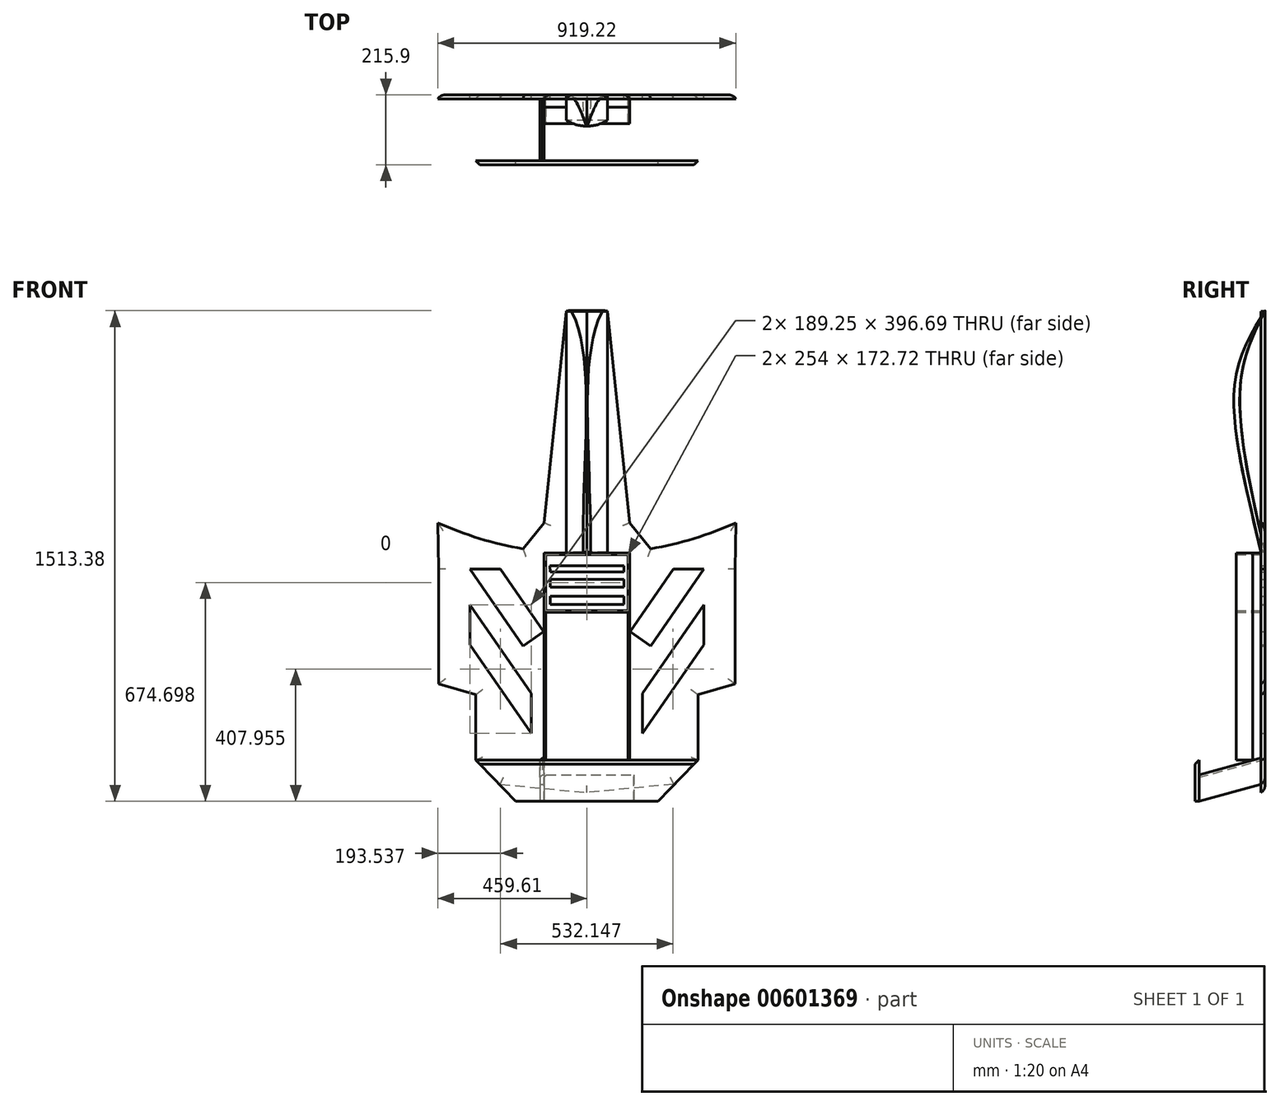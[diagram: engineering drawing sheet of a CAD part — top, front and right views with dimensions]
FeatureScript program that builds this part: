
annotation { "Feature Type Name" : "Feature", "Feature Type Description" : "" }
export const myFeature = defineFeature(function(context is Context, id is Id, definition is map)
    precondition{}
    {
        {
            var Q0;
            Q0=qCreatedBy(makeId("Front.planeOp"),FACE);
            var sketch = newSketch(context, id + "F0", { "sketchPlane" : qUnion([Q0])});
            skLineSegment(sketch, "E0.bottom", {"start": v(-87.15, 1010.87) * mm, "end": v(0, 1010.87) * mm});
            skLineSegment(sketch, "E0.top", {"start": v(-342.9, -81.33) * mm, "end": v(0, -81.33) * mm});
            skLineSegment(sketch, "E0.left", {"start": v(-457.2, 439.97) * mm, "end": v(-457.2, 86.3) * mm});
            skLineSegment(sketch, "E0.right", {"start": v(0, 1010.87) * mm, "end": v(0, -81.33) * mm});
            skLineSegment(sketch, "E1", {"start": v(-457.2, 86.3) * mm, "end": v(-342.9, 52.88) * mm});
            skLineSegment(sketch, "E2", {"start": v(-342.9, 52.88) * mm, "end": v(-342.9, -81.33) * mm});
            skPoint(sketch, "E3.start.orphan", {"position": v(-457.2, 502.87) * mm});
            skPoint(sketch, "E4.start.orphan", {"position": v(-197.03, 542.03) * mm});
            skLineSegment(sketch, "E5", {"start": v(-197.03, 502.87) * mm, "end": v(-132.27, 582.92) * mm});
            skLineSegment(sketch, "E6", {"start": v(-132.27, 582.92) * mm, "end": v(-87.15, 1010.87) * mm});
            skPoint(sketch, "E7.orphan", {"position": v(-457.2, -81.33) * mm});
            skLineSegment(sketch, "E8.MirrorCS", {"start": v(197.03, 502.87) * mm, "end": v(132.27, 582.92) * mm});
            skPoint(sketch, "E9.MirrorP", {"position": v(197.03, 542.03) * mm});
            skLineSegment(sketch, "E10.MirrorCS", {"start": v(87.15, 1010.87) * mm, "end": v(0, 1010.87) * mm});
            skLineSegment(sketch, "E11.MirrorCS", {"start": v(342.9, 52.88) * mm, "end": v(342.9, -81.33) * mm});
            skLineSegment(sketch, "E12.MirrorCS", {"start": v(457.2, 86.3) * mm, "end": v(342.9, 52.88) * mm});
            skPoint(sketch, "E13.MirrorP", {"position": v(457.2, -81.33) * mm});
            skPoint(sketch, "E14.MirrorP", {"position": v(457.2, 502.87) * mm});
            skLineSegment(sketch, "E15.MirrorCS", {"start": v(342.9, -81.33) * mm, "end": v(0, -81.33) * mm});
            skLineSegment(sketch, "E16.MirrorCS", {"start": v(457.2, 439.97) * mm, "end": v(457.2, 86.3) * mm});
            skLineSegment(sketch, "E17.MirrorCS", {"start": v(132.27, 582.92) * mm, "end": v(87.15, 1010.87) * mm});
            skArc(sketch, "E18", {"start": v(-197.03, 502.87) * mm, "mid": v(-330.75, 534.92) * mm, "end": v(-459.6, 582.92) * mm});
            skLineSegment(sketch, "E19", {"start": v(-457.2, 439.97) * mm, "end": v(-459.6, 582.92) * mm});
            skPoint(sketch, "E20.center.orphan", {"position": v(-457.2, 1010.87) * mm});
            skArc(sketch, "E21.MirrorCS", {"start": v(197.03, 502.87) * mm, "mid": v(330.75, 534.92) * mm, "end": v(459.6, 582.92) * mm});
            skLineSegment(sketch, "E22.MirrorCS", {"start": v(457.2, 439.97) * mm, "end": v(459.6, 582.92) * mm});
            skLineSegment(sketch, "E23", {"start": v(132.27, 582.92) * mm, "end": v(63.5, 1235.16) * mm});
            skLineSegment(sketch, "E24", {"start": v(0, 1235.16) * mm, "end": v(63.5, 1235.16) * mm});
            skLineSegment(sketch, "E25", {"start": v(0, 1235.16) * mm, "end": v(-63.5, 1235.16) * mm});
            skPoint(sketch, "E26.orphan", {"position": v(-63.5, 1235.16) * mm});
            skLineSegment(sketch, "E27", {"start": v(-63.5, 1235.16) * mm, "end": v(-87.15, 1010.87) * mm});
            skLineSegment(sketch, "E28", {"start": v(0, -81.33) * mm, "end": v(0, -248.97) * mm});
            skLineSegment(sketch, "E29", {"start": v(-342.9, -81.33) * mm, "end": v(-342.9, -148.64) * mm});
            skLineSegment(sketch, "E30", {"start": v(-267.1, -223.25) * mm, "end": v(0, -248.97) * mm});
            skPoint(sketch, "E31.end.orphan", {"position": v(-267.1, -215.95) * mm});
            skLineSegment(sketch, "E32", {"start": v(-342.9, -148.64) * mm, "end": v(-267.1, -223.25) * mm});
            skPoint(sketch, "E33.orphan", {"position": v(-342.9, -215.95) * mm});
            skLineSegment(sketch, "E34.MirrorCS", {"start": v(342.9, -81.33) * mm, "end": v(342.9, -148.64) * mm});
            skLineSegment(sketch, "E35.MirrorCS", {"start": v(342.9, -148.64) * mm, "end": v(267.1, -223.25) * mm});
            skLineSegment(sketch, "E36.MirrorCS", {"start": v(267.1, -223.25) * mm, "end": v(0, -248.97) * mm});
            skLineSegment(sketch, "E37", {"start": v(197.03, 203.43) * mm, "end": v(133.45, 247.43) * mm});
            skLineSegment(sketch, "E38", {"start": v(133.45, 247.43) * mm, "end": v(266.67, 439.97) * mm});
            skLineSegment(sketch, "E39", {"start": v(266.67, 439.97) * mm, "end": v(360.7, 439.97) * mm});
            skLineSegment(sketch, "E40.MirrorCS", {"start": v(-133.45, 247.43) * mm, "end": v(-266.67, 439.97) * mm});
            skLineSegment(sketch, "E41.MirrorCS", {"start": v(-197.03, 203.43) * mm, "end": v(-133.45, 247.43) * mm});
            skLineSegment(sketch, "E42.MirrorCS", {"start": v(-266.67, 439.97) * mm, "end": v(-360.7, 439.97) * mm});
            skLineSegment(sketch, "E43", {"start": v(360.7, 439.97) * mm, "end": v(197.03, 203.43) * mm});
            skLineSegment(sketch, "E44", {"start": v(-360.7, 439.97) * mm, "end": v(-197.03, 203.43) * mm});
            skLineSegment(sketch, "E45", {"start": v(171.45, 57.15) * mm, "end": v(360.7, 330.66) * mm});
            skPoint(sketch, "E45.startSnap0", {"position": v(171.45, -81.33) * mm});
            skLineSegment(sketch, "E46", {"start": v(360.7, 330.66) * mm, "end": v(360.7, 207.48) * mm});
            skLineSegment(sketch, "E47", {"start": v(360.7, 207.48) * mm, "end": v(171.45, -66.03) * mm});
            skLineSegment(sketch, "E48", {"start": v(171.45, 57.15) * mm, "end": v(171.45, -66.03) * mm});
            skLineSegment(sketch, "E49.MirrorCS", {"start": v(-171.45, 57.15) * mm, "end": v(-360.7, 330.66) * mm});
            skLineSegment(sketch, "E50.MirrorCS", {"start": v(-360.7, 207.48) * mm, "end": v(-171.45, -66.03) * mm});
            skLineSegment(sketch, "E51.MirrorCS", {"start": v(-171.45, 57.15) * mm, "end": v(-171.45, -66.03) * mm});
            skLineSegment(sketch, "E52.MirrorCS", {"start": v(-360.7, 330.66) * mm, "end": v(-360.7, 207.48) * mm});
            skLineSegment(sketch, "E53", {"start": v(-114.3, 450.83) * mm, "end": v(114.3, 450.83) * mm});
            skLineSegment(sketch, "E54", {"start": v(114.3, 450.83) * mm, "end": v(114.3, 431.4) * mm});
            skLineSegment(sketch, "E55", {"start": v(114.3, 431.4) * mm, "end": v(-112.92, 431.4) * mm});
            skLineSegment(sketch, "E56", {"start": v(-112.92, 431.4) * mm, "end": v(-114.3, 450.83) * mm});
            skLineSegment(sketch, "E57", {"start": v(-112.92, 408.42) * mm, "end": v(-112.92, 384.28) * mm});
            skLineSegment(sketch, "E58", {"start": v(-112.92, 384.28) * mm, "end": v(114.3, 384.28) * mm});
            skLineSegment(sketch, "E59", {"start": v(114.3, 384.28) * mm, "end": v(114.3, 408.42) * mm});
            skLineSegment(sketch, "E60", {"start": v(114.3, 408.42) * mm, "end": v(-112.92, 408.42) * mm});
            skLineSegment(sketch, "E61", {"start": v(-112.92, 356.37) * mm, "end": v(-112.92, 330.7) * mm});
            skLineSegment(sketch, "E62", {"start": v(-112.92, 330.7) * mm, "end": v(114.3, 330.7) * mm});
            skLineSegment(sketch, "E63", {"start": v(114.3, 330.7) * mm, "end": v(114.3, 356.37) * mm});
            skLineSegment(sketch, "E64", {"start": v(114.3, 356.37) * mm, "end": v(-112.92, 356.37) * mm});
            skSolve(sketch);
        }
        {
            var Q0;
            Q0=qCreatedBy(makeId("Right.planeOp"),FACE);
            var sketch = newSketch(context, id + "F1", { "sketchPlane" : qUnion([Q0])});
            skLineSegment(sketch, "E65", {"start": v(0, -172.72) * mm, "end": v(-76.2, -172.72) * mm});
            skLineSegment(sketch, "E66", {"start": v(-76.2, -172.72) * mm, "end": v(-76.2, 0) * mm});
            skLineSegment(sketch, "E67", {"start": v(-76.2, 0) * mm, "end": v(0, 0) * mm});
            skLineSegment(sketch, "E68", {"start": v(0, 492.63) * mm, "end": v(-12.7, 492.63) * mm});
            skPoint(sketch, "E69.center.orphan", {"position": v(0, 1010.95) * mm});
            skPoint(sketch, "E70.center.orphan", {"position": v(0, -148.77) * mm});
            skFitSpline(sketch, "E71", {"points": [v(0, 492.63) * mm, v(-76.2, 1010.95) * mm, v(0, 1236.69) * mm], "startDerivative": vector(-222.18, 959.65) * mm, "endDerivative": vector(252.99, 498.58) * mm});
            skFitSpline(sketch, "E72", {"points": [v(0, 1237.74) * mm, v(-93.66, 1010.95) * mm, v(-12.7, 492.63) * mm], "startDerivative": vector(-301.04, -493.75) * mm, "endDerivative": vector(220.2, -966.97) * mm});
            skLineSegment(sketch, "E73", {"start": v(-12.7, 492.63) * mm, "end": v(-12.7, -249.15) * mm});
            skLineSegment(sketch, "E74", {"start": v(0, -249.15) * mm, "end": v(-12.7, -249.15) * mm});
            skPoint(sketch, "E75.end.orphan", {"position": v(0, -250.54) * mm});
            skPoint(sketch, "E76.orphan", {"position": v(-12.7, -250.54) * mm});
            skLineSegment(sketch, "E77", {"start": v(0, 492.63) * mm, "end": v(0, -249.15) * mm});
            skLineSegment(sketch, "E78", {"start": v(0, 1236.69) * mm, "end": v(0, 1237.74) * mm});
            skPoint(sketch, "E79.end.orphan", {"position": v(0, -426.72) * mm});
            skPoint(sketch, "E79.start.orphan", {"position": v(-76.2, -426.72) * mm});
            skSolve(sketch);
        }
        {
            var Q0;
            Q0=makeQuery(id+"F0.imprint","IMPRINT",FACE,{"disambiguationData":[TD([[makeQuery(id+"F0.imprint","IMPRINT",EDGE,{"derivedFrom":sQuery(id+"F0.wireOp",EDGE,"E0.right")}),1.0]])]});
            var Q1;
            Q1=makeQuery(id+"F0.imprint","IMPRINT",FACE,{"disambiguationData":[TD([[makeQuery(id+"F0.imprint","IMPRINT",EDGE,{"derivedFrom":sQuery(id+"F0.wireOp",EDGE,"E0.bottom")}),-1.0]])]});
            var Q2;
            Q2=makeQuery(id+"F0.imprint","IMPRINT",FACE,{"disambiguationData":[TD([[makeQuery(id+"F0.imprint","IMPRINT",EDGE,{"derivedFrom":sQuery(id+"F0.wireOp",EDGE,"E0.top")}),-1.0]])]});
            var Q3;
            Q3=makeQuery(id+"F0.imprint","IMPRINT",FACE,{"disambiguationData":[TD([[makeQuery(id+"F0.imprint","IMPRINT",EDGE,{"derivedFrom":sQuery(id+"F0.wireOp",EDGE,"E15.MirrorCS")}),1.0]])]});
            var Q4;
            Q4=makeQuery(id+"F0.imprint","IMPRINT",FACE,{"disambiguationData":[TD([[makeQuery(id+"F0.imprint","IMPRINT",EDGE,{"derivedFrom":sQuery(id+"F0.wireOp",EDGE,"E0.bottom")}),1.0]])]});
            extrude(context, id + "F2", {"entities" : qUnion([Q0, Q1, Q2, Q3, Q4]), "depth" : 12.7 * mm, "offsetDistance" : 25.4 * mm, "hasSecondDirection" : true, "secondDirectionOppositeDirection" : false, "secondDirectionDepth" : 0 * mm});
        }
        {
            var Q0;
            Q0=makeQuery(id+"F1.imprint","IMPRINT",FACE,{"disambiguationData":[TD([[makeQuery(id+"F1.imprint","IMPRINT",EDGE,{"derivedFrom":sQuery(id+"F1.wireOp",EDGE,"E68")}),-1.0]])]});
            extrude(context, id + "F3", {"entities" : qUnion([Q0]), "depth" : 63.5 * mm, "offsetDistance" : 25.4 * mm});
        }
        {
            var Q0;
            Q0=makeQuery(id+"F3.opExtrude","CAP_FACE",FACE,{"disambiguationData":[OSD([sQuery(id+"F1.wireOp",EDGE,"E68"),sQuery(id+"F1.wireOp",EDGE,"E71"),sQuery(id+"F1.wireOp",EDGE,"E72"),sQuery(id+"F1.wireOp",EDGE,"E78")])],"isStart":true});
            extrude(context, id + "F4", {"entities" : qUnion([Q0]), "depth" : 63.5 * mm, "offsetDistance" : 25.4 * mm});
        }
        {
            var Q0;
            Q0=makeQuery(id+"F2.opExtrude","CAP_FACE",FACE,{"disambiguationData":[OSD([sQuery(id+"F0.wireOp",EDGE,"E0.left"),sQuery(id+"F0.wireOp",EDGE,"E1"),sQuery(id+"F0.wireOp",EDGE,"E2"),sQuery(id+"F0.wireOp",EDGE,"E5"),sQuery(id+"F0.wireOp",EDGE,"E8.MirrorCS"),sQuery(id+"F0.wireOp",EDGE,"E11.MirrorCS"),sQuery(id+"F0.wireOp",EDGE,"E12.MirrorCS"),sQuery(id+"F0.wireOp",EDGE,"E16.MirrorCS"),sQuery(id+"F0.wireOp",EDGE,"E18"),sQuery(id+"F0.wireOp",EDGE,"E19"),sQuery(id+"F0.wireOp",EDGE,"E21.MirrorCS"),sQuery(id+"F0.wireOp",EDGE,"E22.MirrorCS"),sQuery(id+"F0.wireOp",EDGE,"E6"),sQuery(id+"F0.wireOp",EDGE,"E23"),sQuery(id+"F0.wireOp",EDGE,"E24"),sQuery(id+"F0.wireOp",EDGE,"E25"),sQuery(id+"F0.wireOp",EDGE,"E27"),sQuery(id+"F0.wireOp",EDGE,"E29"),sQuery(id+"F0.wireOp",EDGE,"E30"),sQuery(id+"F0.wireOp",EDGE,"E32"),sQuery(id+"F0.wireOp",EDGE,"E34.MirrorCS"),sQuery(id+"F0.wireOp",EDGE,"E35.MirrorCS"),sQuery(id+"F0.wireOp",EDGE,"E36.MirrorCS")])],"isStart":false});
            var sketch = newSketch(context, id + "F5", { "sketchPlane" : qUnion([Q0])});
            skLineSegment(sketch, "E80", {"start": v(0, 485.42) * mm, "end": v(-127, 485.42) * mm});
            skLineSegment(sketch, "E81", {"start": v(-127, 485.42) * mm, "end": v(-127, 312.7) * mm});
            skLineSegment(sketch, "E82", {"start": v(-127, 312.7) * mm, "end": v(127, 312.7) * mm});
            skLineSegment(sketch, "E83", {"start": v(127, 312.7) * mm, "end": v(127, 485.42) * mm});
            skLineSegment(sketch, "E84", {"start": v(127, 485.42) * mm, "end": v(0, 485.42) * mm});
            skLineSegment(sketch, "E85", {"start": v(-132.08, 485.42) * mm, "end": v(-132.08, 307.62) * mm});
            skLineSegment(sketch, "E86", {"start": v(-132.08, 307.62) * mm, "end": v(132.08, 307.62) * mm});
            skLineSegment(sketch, "E87", {"start": v(132.08, 307.62) * mm, "end": v(132.08, 490.5) * mm});
            skLineSegment(sketch, "E88", {"start": v(132.08, 490.5) * mm, "end": v(-132.08, 490.5) * mm});
            skLineSegment(sketch, "E89", {"start": v(-132.08, 490.5) * mm, "end": v(-132.08, 485.42) * mm});
            skLineSegment(sketch, "E90", {"start": v(132.08, 307.62) * mm, "end": v(132.08, -236.25) * mm});
            skLineSegment(sketch, "E91", {"start": v(-132.08, 307.62) * mm, "end": v(-132.08, -236.25) * mm});
            skLineSegment(sketch, "E92", {"start": v(-127, 312.7) * mm, "end": v(-127, -236.25) * mm});
            skLineSegment(sketch, "E93", {"start": v(127, 312.7) * mm, "end": v(127, -90.76) * mm});
            skLineSegment(sketch, "E94", {"start": v(127, -90.76) * mm, "end": v(127, -236.25) * mm});
            skLineSegment(sketch, "E95", {"start": v(-132.08, -236.25) * mm, "end": v(-127, -236.25) * mm});
            skLineSegment(sketch, "E96", {"start": v(127, -236.25) * mm, "end": v(132.08, -236.25) * mm});
            skSolve(sketch);
        }
        {
            var Q0;
            Q0=makeQuery(id+"F5.imprint","IMPRINT",FACE,{"disambiguationData":[TD([[makeQuery(id+"F5.imprint","IMPRINT",EDGE,{"derivedFrom":sQuery(id+"F5.wireOp",EDGE,"E80")}),1.0]])]});
            extrude(context, id + "F6", {"entities" : qUnion([Q0]), "operationType" : NewBodyOperationType.REMOVE, "depth" : 76.2 * mm, "offsetDistance" : 25.4 * mm});
        }
        {
            var Q0;
            Q0 = qSketchRegion(id + "F5", true);
            extrude(context, id + "F7", {"entities" : qUnion([Q0]), "depth" : 76.2 * mm, "offsetDistance" : 25.4 * mm});
        }
        {
            var Q0;
            Q0 = qSketchRegion(id + "F5", true);
            extrude(context, id + "F8", {"entities" : qUnion([Q0]), "depth" : 25.4 * mm, "offsetDistance" : 25.4 * mm});
        }
        {
            var Q0;
            Q0=makeQuery(id+"F2.opExtrude","CAP_FACE",FACE,{"disambiguationData":[OSD([sQuery(id+"F0.wireOp",EDGE,"E0.left"),sQuery(id+"F0.wireOp",EDGE,"E1"),sQuery(id+"F0.wireOp",EDGE,"E2"),sQuery(id+"F0.wireOp",EDGE,"E5"),sQuery(id+"F0.wireOp",EDGE,"E8.MirrorCS"),sQuery(id+"F0.wireOp",EDGE,"E11.MirrorCS"),sQuery(id+"F0.wireOp",EDGE,"E12.MirrorCS"),sQuery(id+"F0.wireOp",EDGE,"E16.MirrorCS"),sQuery(id+"F0.wireOp",EDGE,"E18"),sQuery(id+"F0.wireOp",EDGE,"E19"),sQuery(id+"F0.wireOp",EDGE,"E21.MirrorCS"),sQuery(id+"F0.wireOp",EDGE,"E22.MirrorCS"),sQuery(id+"F0.wireOp",EDGE,"E6"),sQuery(id+"F0.wireOp",EDGE,"E23"),sQuery(id+"F0.wireOp",EDGE,"E24"),sQuery(id+"F0.wireOp",EDGE,"E25"),sQuery(id+"F0.wireOp",EDGE,"E27"),sQuery(id+"F0.wireOp",EDGE,"E29"),sQuery(id+"F0.wireOp",EDGE,"E30"),sQuery(id+"F0.wireOp",EDGE,"E32"),sQuery(id+"F0.wireOp",EDGE,"E34.MirrorCS"),sQuery(id+"F0.wireOp",EDGE,"E35.MirrorCS"),sQuery(id+"F0.wireOp",EDGE,"E36.MirrorCS"),sQuery(id+"F0.wireOp",EDGE,"E37"),sQuery(id+"F0.wireOp",EDGE,"E38"),sQuery(id+"F0.wireOp",EDGE,"E39"),sQuery(id+"F0.wireOp",EDGE,"E40.MirrorCS"),sQuery(id+"F0.wireOp",EDGE,"E41.MirrorCS"),sQuery(id+"F0.wireOp",EDGE,"E42.MirrorCS"),sQuery(id+"F0.wireOp",EDGE,"E43"),sQuery(id+"F0.wireOp",EDGE,"E44"),sQuery(id+"F0.wireOp",EDGE,"E45"),sQuery(id+"F0.wireOp",EDGE,"E46"),sQuery(id+"F0.wireOp",EDGE,"E47"),sQuery(id+"F0.wireOp",EDGE,"E48"),sQuery(id+"F0.wireOp",EDGE,"E49.MirrorCS"),sQuery(id+"F0.wireOp",EDGE,"E50.MirrorCS"),sQuery(id+"F0.wireOp",EDGE,"E51.MirrorCS"),sQuery(id+"F0.wireOp",EDGE,"E52.MirrorCS"),sQuery(id+"F0.wireOp",EDGE,"E53"),sQuery(id+"F0.wireOp",EDGE,"E54"),sQuery(id+"F0.wireOp",EDGE,"E55"),sQuery(id+"F0.wireOp",EDGE,"E56"),sQuery(id+"F0.wireOp",EDGE,"E57"),sQuery(id+"F0.wireOp",EDGE,"E58"),sQuery(id+"F0.wireOp",EDGE,"E59"),sQuery(id+"F0.wireOp",EDGE,"E60"),sQuery(id+"F0.wireOp",EDGE,"E61"),sQuery(id+"F0.wireOp",EDGE,"E62"),sQuery(id+"F0.wireOp",EDGE,"E63"),sQuery(id+"F0.wireOp",EDGE,"E64")])],"isStart":false});
            var sketch = newSketch(context, id + "F9", { "sketchPlane" : qUnion([Q0])});
            skLineSegment(sketch, "E97", {"start": v(-342.9, -148.64) * mm, "end": v(342.9, -148.64) * mm});
            skLineSegment(sketch, "E98", {"start": v(-342.9, -148.64) * mm, "end": v(-219.33, -275.64) * mm});
            skLineSegment(sketch, "E99", {"start": v(342.9, -148.64) * mm, "end": v(220.01, -275.64) * mm});
            skLineSegment(sketch, "E100", {"start": v(-219.33, -275.64) * mm, "end": v(220.01, -275.64) * mm});
            skSolve(sketch);
        }
        {
            var Q0;
            Q0 = qSketchRegion(id + "F9", true);
            extrude(context, id + "F10", {"entities" : qUnion([Q0]), "depth" : 203.2 * mm, "offsetDistance" : 25.4 * mm});
        }
        {
            var Q0;
            Q0=makeQuery(id+"F10.opExtrude","CAP_FACE",FACE,{"disambiguationData":[OSD([sQuery(id+"F9.wireOp",EDGE,"E97"),sQuery(id+"F9.wireOp",EDGE,"E98"),sQuery(id+"F9.wireOp",EDGE,"E99"),sQuery(id+"F9.wireOp",EDGE,"E100")])],"isStart":true});
            extrude(context, id + "F11", {"entities" : qUnion([Q0]), "operationType" : NewBodyOperationType.REMOVE, "oppositeDirection" : true, "depth" : 190.5 * mm, "offsetDistance" : 25.4 * mm});
        }
        {
            var Q0;
            Q0=makeQuery(id+"F7.opExtrude","SWEPT_FACE",FACE,{"disambiguationData":[OSD([sQuery(id+"F5.wireOp",EDGE,"E87"),sQuery(id+"F5.wireOp",EDGE,"E90")])]});
            var sketch = newSketch(context, id + "F12", { "sketchPlane" : qUnion([Q0])});
            skLineSegment(sketch, "E101", {"start": v(-12.7, -223.36) * mm, "end": v(-202.24, -274.9) * mm});
            skLineSegment(sketch, "E102", {"start": v(-202.24, -193.63) * mm, "end": v(-12.7, -142.08) * mm});
            skLineSegment(sketch, "E103", {"start": v(-12.7, -142.08) * mm, "end": v(-12.7, -223.36) * mm});
            skLineSegment(sketch, "E104", {"start": v(-202.24, -193.63) * mm, "end": v(-204.78, -194.32) * mm});
            skLineSegment(sketch, "E105", {"start": v(-204.78, -194.32) * mm, "end": v(-204.78, -275.6) * mm});
            skLineSegment(sketch, "E106", {"start": v(-202.24, -274.9) * mm, "end": v(-204.78, -275.6) * mm});
            skLineSegment(sketch, "E107", {"start": v(-204.78, -275.6) * mm, "end": v(-204.78, -275.6) * mm});
            skSolve(sketch);
        }
        {
            var Q0;
            Q0 = qSketchRegion(id + "F12", true);
            extrude(context, id + "F13", {"entities" : qUnion([Q0]), "depth" : 12.7 * mm, "offsetDistance" : 25.4 * mm});
        }
        {
            var Q0;
            Q0 = qSketchRegion(id + "F12", true);
            extrude(context, id + "F14", {"entities" : qUnion([Q0]), "oppositeDirection" : true, "depth" : 276.86 * mm, "offsetDistance" : 25.4 * mm});
        }
        {
            var Q0;
            Q0=makeQuery(id+"F13.opExtrude","CAP_FACE",FACE,{"disambiguationData":[OSD([sQuery(id+"F12.wireOp",EDGE,"E101"),sQuery(id+"F12.wireOp",EDGE,"E102"),sQuery(id+"F12.wireOp",EDGE,"E103"),sQuery(id+"F12.wireOp",EDGE,"E104"),sQuery(id+"F12.wireOp",EDGE,"E105"),sQuery(id+"F12.wireOp",EDGE,"E106")])],"isStart":false});
            extrude(context, id + "F15", {"entities" : qUnion([Q0]), "operationType" : NewBodyOperationType.REMOVE, "oppositeDirection" : true, "depth" : 276.86 * mm, "offsetDistance" : 25.4 * mm});
        }
        {
            var Q0;
            Q0=makeQuery(id+"F3.opExtrude","CAP_EDGE",EDGE,{"disambiguationData":[OSD([sQuery(id+"F1.wireOp",EDGE,"E72")])],"isStart":false});
            var Q1;
            Q1=makeQuery(id+"F4.opExtrude","CAP_EDGE",EDGE,{"disambiguationData":[OSD([sQuery(id+"F1.wireOp",EDGE,"E72")])],"isStart":false});
            fillet(context, id + "F16", {"entities" : qUnion([Q0, Q1]), "radius" : 114.3 * mm, "tangentPropagation" : true, "allowEdgeOverflow" : false});
        }
        {
            var Q0;
            Q0=makeQuery(id+"F2.opExtrude","CAP_EDGE",EDGE,{"disambiguationData":[OSD([sQuery(id+"F0.wireOp",EDGE,"E6"),sQuery(id+"F0.wireOp",EDGE,"E27")])],"isStart":true});
            var Q1;
            Q1=makeQuery(id+"F2.opExtrude","CAP_EDGE",EDGE,{"disambiguationData":[OSD([sQuery(id+"F0.wireOp",EDGE,"E23")])],"isStart":true});
            var Q2;
            Q2=makeQuery(id+"F2.opExtrude","CAP_EDGE",EDGE,{"disambiguationData":[OSD([sQuery(id+"F0.wireOp",EDGE,"E8.MirrorCS")])],"isStart":true});
            var Q3;
            Q3=makeQuery(id+"F2.opExtrude","CAP_EDGE",EDGE,{"disambiguationData":[OSD([sQuery(id+"F0.wireOp",EDGE,"E21.MirrorCS")])],"isStart":true});
            var Q4;
            Q4=makeQuery(id+"F2.opExtrude","CAP_EDGE",EDGE,{"disambiguationData":[OSD([sQuery(id+"F0.wireOp",EDGE,"E22.MirrorCS")])],"isStart":true});
            var Q5;
            Q5=makeQuery(id+"F2.opExtrude","CAP_EDGE",EDGE,{"disambiguationData":[OSD([sQuery(id+"F0.wireOp",EDGE,"E12.MirrorCS")])],"isStart":true});
            var Q6;
            Q6=makeQuery(id+"F2.opExtrude","CAP_EDGE",EDGE,{"disambiguationData":[OSD([sQuery(id+"F0.wireOp",EDGE,"E11.MirrorCS"),sQuery(id+"F0.wireOp",EDGE,"E34.MirrorCS")])],"isStart":true});
            var Q7;
            Q7=makeQuery(id+"F2.opExtrude","CAP_EDGE",EDGE,{"disambiguationData":[OSD([sQuery(id+"F0.wireOp",EDGE,"E5")])],"isStart":true});
            var Q8;
            Q8=makeQuery(id+"F2.opExtrude","CAP_EDGE",EDGE,{"disambiguationData":[OSD([sQuery(id+"F0.wireOp",EDGE,"E18")])],"isStart":true});
            var Q9;
            Q9=makeQuery(id+"F2.opExtrude","CAP_EDGE",EDGE,{"disambiguationData":[OSD([sQuery(id+"F0.wireOp",EDGE,"E19")])],"isStart":true});
            var Q10;
            Q10=makeQuery(id+"F2.opExtrude","CAP_EDGE",EDGE,{"disambiguationData":[OSD([sQuery(id+"F0.wireOp",EDGE,"E1")])],"isStart":true});
            var Q11;
            Q11=makeQuery(id+"F2.opExtrude","CAP_EDGE",EDGE,{"disambiguationData":[OSD([sQuery(id+"F0.wireOp",EDGE,"E2"),sQuery(id+"F0.wireOp",EDGE,"E29")])],"isStart":true});
            var Q12;
            Q12=makeQuery(id+"F2.opExtrude","CAP_EDGE",EDGE,{"disambiguationData":[OSD([sQuery(id+"F0.wireOp",EDGE,"E32")])],"isStart":true});
            var Q13;
            Q13=makeQuery(id+"F2.opExtrude","CAP_EDGE",EDGE,{"disambiguationData":[OSD([sQuery(id+"F0.wireOp",EDGE,"E30")])],"isStart":true});
            var Q14;
            Q14=makeQuery(id+"F2.opExtrude","CAP_EDGE",EDGE,{"disambiguationData":[OSD([sQuery(id+"F0.wireOp",EDGE,"E36.MirrorCS")])],"isStart":true});
            var Q15;
            Q15=makeQuery(id+"F2.opExtrude","CAP_EDGE",EDGE,{"disambiguationData":[OSD([sQuery(id+"F0.wireOp",EDGE,"E35.MirrorCS")])],"isStart":true});
            fillet(context, id + "F17", {"entities" : qUnion([Q0, Q1, Q2, Q3, Q4, Q5, Q6, Q7, Q8, Q9, Q10, Q11, Q12, Q13, Q14, Q15]), "radius" : 25.4 * mm, "tangentPropagation" : true, "allowEdgeOverflow" : false});
        }
        {
            var Q0;
            Q0=makeQuery(id+"F10.opExtrude","CAP_EDGE",EDGE,{"disambiguationData":[OSD([sQuery(id+"F9.wireOp",EDGE,"E97")])],"isStart":false});
            chamfer(context, id + "F18", {"entities" : qUnion([Q0]), "width" : 12.7 * mm, "tangentPropagation" : true});
        }
        {
            var Q0;
            Q0=makeQuery(id+"F7.opExtrude","SWEPT_EDGE",EDGE,{"disambiguationData":[OSD([sQuery(id+"F5.wireOp",EDGE,"E87"),sQuery(id+"F5.wireOp",EDGE,"E88")])]});
            var Q1;
            Q1=makeQuery(id+"F7.opExtrude","SWEPT_EDGE",EDGE,{"disambiguationData":[OSD([sQuery(id+"F5.wireOp",EDGE,"E88"),sQuery(id+"F5.wireOp",EDGE,"E89")])]});
            fillet(context, id + "F19", {"entities" : qUnion([Q0, Q1]), "radius" : 5.08 * mm, "tangentPropagation" : true, "allowEdgeOverflow" : false});
        }
        {
            var Q0;
            Q0=makeQuery(id+"F14.opExtrude","CAP_EDGE",EDGE,{"disambiguationData":[OSD([sQuery(id+"F12.wireOp",EDGE,"E102"),sQuery(id+"F12.wireOp",EDGE,"E104")])],"isStart":false});
            var Q1;
            Q1=makeQuery(id+"F15.boolean.opBoolean","COPY",EDGE,{"derivedFrom":makeQuery(id+"F15.opExtrude","CAP_EDGE",EDGE,{"disambiguationData":[OSD([sQuery(id+"F12.wireOp",EDGE,"E102"),sQuery(id+"F12.wireOp",EDGE,"E104")])],"isStart":false})});
            var Q2;
            Q2=makeQuery(id+"F13.opExtrude","CAP_EDGE",EDGE,{"disambiguationData":[OSD([sQuery(id+"F12.wireOp",EDGE,"E102"),sQuery(id+"F12.wireOp",EDGE,"E104")])],"isStart":true});
            var Q3;
            Q3=makeQuery(id+"F13.opExtrude","CAP_EDGE",EDGE,{"disambiguationData":[OSD([sQuery(id+"F12.wireOp",EDGE,"E102"),sQuery(id+"F12.wireOp",EDGE,"E104")])],"isStart":false});
            chamfer(context, id + "F20", {"entities" : qUnion([Q0, Q1, Q2, Q3]), "width" : 7.62 * mm, "tangentPropagation" : true});
        }
    });
